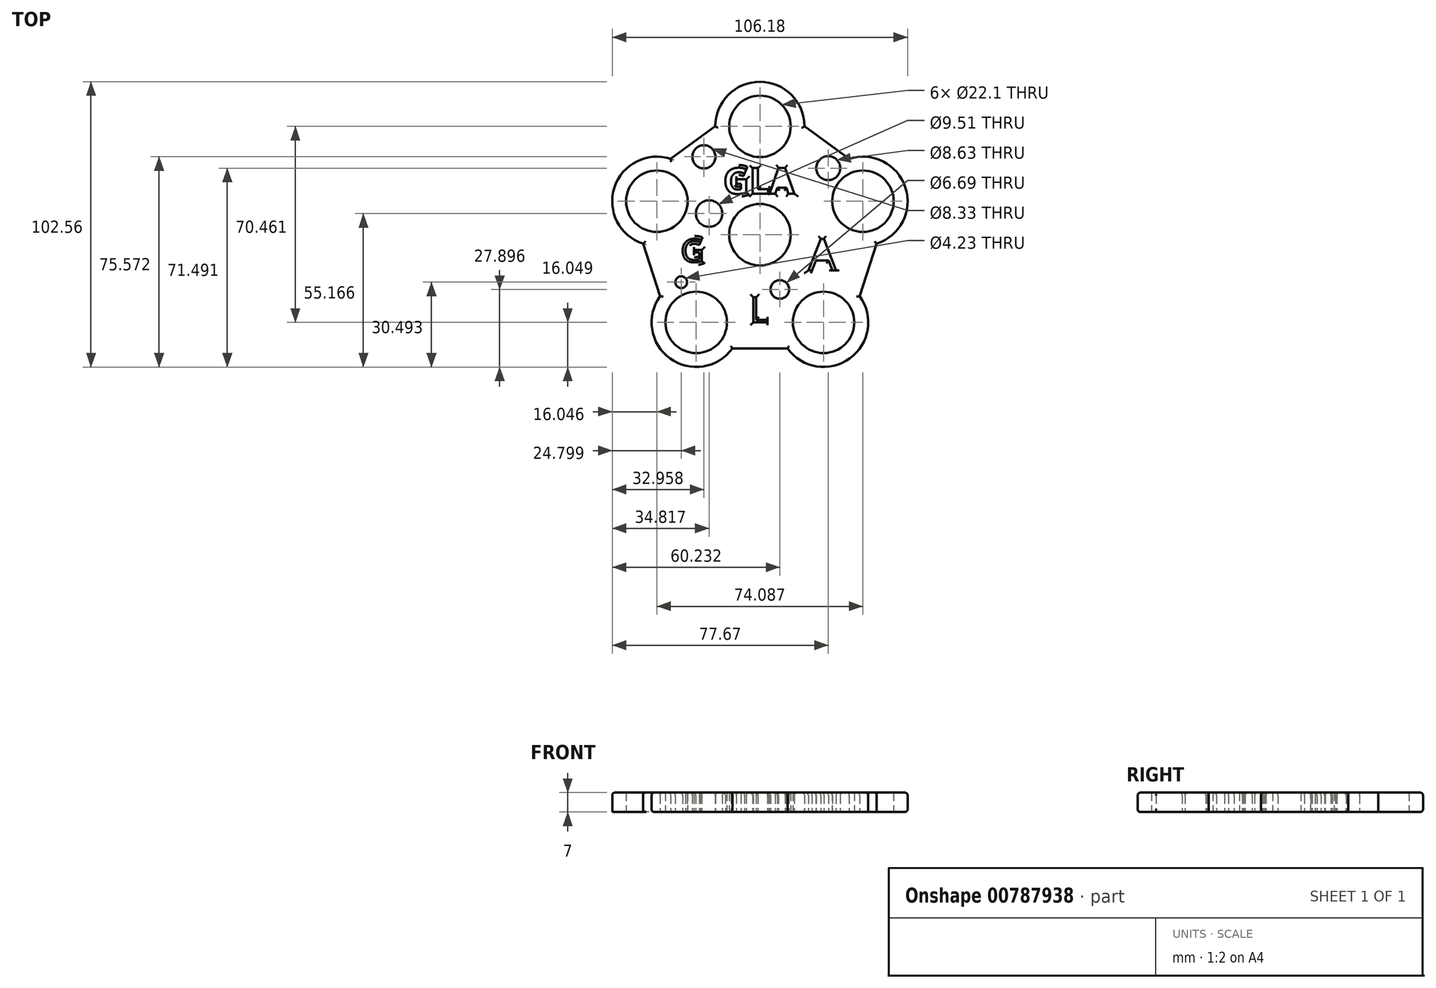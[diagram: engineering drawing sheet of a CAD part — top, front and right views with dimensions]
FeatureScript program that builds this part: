
annotation { "Feature Type Name" : "Feature", "Feature Type Description" : "" }
export const myFeature = defineFeature(function(context is Context, id is Id, definition is map)
    precondition{}
    {
        {
            var Q0;
            Q0=qCreatedBy(makeId("Top.planeOp"),FACE);
            var sketch = newSketch(context, id + "F0", { "sketchPlane" : qUnion([Q0])});
            skCircle(sketch, "E0", {"center": v(0, 0) * mm, "radius": 11.05 * mm});
            skCircle(sketch, "E1", {"center": v(0, 38.95) * mm, "radius": 11.05 * mm});
            skArc(sketch, "E2", {"start": v(16.05, 38.95) * mm, "mid": v(0, 55) * mm, "end": v(-16.05, 38.95) * mm});
            skCircle(sketch, "E3.1.0", {"center": v(-37.04, 12.04) * mm, "radius": 11.05 * mm});
            skArc(sketch, "E3.1.1", {"start": v(-32.08, 27.3) * mm, "mid": v(-52.3, 17) * mm, "end": v(-42, -3.23) * mm});
            skCircle(sketch, "E3.2.0", {"center": v(-22.9, -31.51) * mm, "radius": 11.05 * mm});
            skArc(sketch, "E3.2.1", {"start": v(-35.88, -22.08) * mm, "mid": v(-32.33, -44.5) * mm, "end": v(-9.9, -40.95) * mm});
            skCircle(sketch, "E3.3.0", {"center": v(22.9, -31.51) * mm, "radius": 11.05 * mm});
            skArc(sketch, "E3.3.1", {"start": v(9.9, -40.95) * mm, "mid": v(32.33, -44.5) * mm, "end": v(35.88, -22.08) * mm});
            skCircle(sketch, "E3.4.0", {"center": v(37.04, 12.04) * mm, "radius": 11.05 * mm});
            skArc(sketch, "E3.4.1", {"start": v(42, -3.23) * mm, "mid": v(52.3, 17) * mm, "end": v(32.08, 27.3) * mm});
            skLineSegment(sketch, "E4", {"start": v(-32.08, 27.3) * mm, "end": v(-32.08, 27.3) * mm});
            skLineSegment(sketch, "E5", {"start": v(-42, -3.23) * mm, "end": v(-35.88, -22.08) * mm, "construction": true});
            skLineSegment(sketch, "E6", {"start": v(-9.9, -40.95) * mm, "end": v(9.9, -40.95) * mm, "construction": true});
            skLineSegment(sketch, "E7", {"start": v(16.05, 38.95) * mm, "end": v(32.08, 27.3) * mm, "construction": true});
            skLineSegment(sketch, "E8", {"start": v(-16.05, 38.95) * mm, "end": v(-16.05, 38.95) * mm});
            skLineSegment(sketch, "E9", {"start": v(-32.08, 27.3) * mm, "end": v(-16.05, 38.95) * mm, "construction": true});
            skLineSegment(sketch, "E10", {"start": v(-32.08, 27.3) * mm, "end": v(-16.05, 38.95) * mm});
            skLineSegment(sketch, "E11", {"start": v(16.05, 38.95) * mm, "end": v(32.08, 27.3) * mm});
            skLineSegment(sketch, "E12", {"start": v(42, -3.23) * mm, "end": v(35.88, -22.08) * mm});
            skLineSegment(sketch, "E13", {"start": v(9.9, -40.95) * mm, "end": v(-9.9, -40.95) * mm});
            skLineSegment(sketch, "E14", {"start": v(-35.88, -22.08) * mm, "end": v(-42, -3.23) * mm});
            skText(sketch, "E15", { "text": "GLA", "fontName": "OpenSans-Bold.ttf"});
            skText(sketch, "E16", { "text": "G", "fontName": "OpenSans-Regular.ttf"});
            skText(sketch, "E17", { "text": "L", "fontName": "OpenSans-Regular.ttf"});
            skText(sketch, "E18", { "text": "A", "fontName": "OpenSans-Regular.ttf"});
            skCircle(sketch, "E19", {"center": v(-18.27, 7.6) * mm, "radius": 4.76 * mm});
            skCircle(sketch, "E20", {"center": v(24.58, 23.93) * mm, "radius": 4.31 * mm});
            skCircle(sketch, "E21", {"center": v(7.14, -19.66) * mm, "radius": 3.34 * mm});
            skCircle(sketch, "E22", {"center": v(-20.13, 28.01) * mm, "radius": 4.17 * mm});
            skCircle(sketch, "E23", {"center": v(-28.3, -17.07) * mm, "radius": 2.12 * mm});
            const initialGuessF0  = {"E15": [-0.01317, 0.01475, 1, 0, 0.00928], "E16": [-0.02848, -0.00983, 1, 0, 0.00835], "E17": [-0.00362, -0.03151, 1, 0, 0.0091], "E18": [0.01742, -0.01285, 1, 0, 0.01134]};
            skSetInitialGuess(sketch, initialGuessF0);
            skSolve(sketch);
        }
        {
            var Q0;
            Q0 = qSketchRegion(id + "F0", true);
            extrude(context, id + "F1", {"entities" : qUnion([Q0]), "depth" : 7 * mm, "offsetDistance" : 25 * mm});
        }
        {
            var Q0;
            Q0=makeQuery(id+"F1.opExtrude","CAP_EDGE",EDGE,{"disambiguationData":[OSD([sQuery(id+"F0.wireOp",EDGE,"E10")])],"isStart":false});
            var Q1;
            Q1=makeQuery(id+"F1.opExtrude","CAP_EDGE",EDGE,{"disambiguationData":[OSD([sQuery(id+"F0.wireOp",EDGE,"E3.1.1")])],"isStart":false});
            var Q2;
            Q2=makeQuery(id+"F1.opExtrude","CAP_EDGE",EDGE,{"disambiguationData":[OSD([sQuery(id+"F0.wireOp",EDGE,"E14")])],"isStart":false});
            var Q3;
            Q3=makeQuery(id+"F1.opExtrude","CAP_EDGE",EDGE,{"disambiguationData":[OSD([sQuery(id+"F0.wireOp",EDGE,"E3.2.1")])],"isStart":false});
            var Q4;
            Q4=makeQuery(id+"F1.opExtrude","CAP_EDGE",EDGE,{"disambiguationData":[OSD([sQuery(id+"F0.wireOp",EDGE,"E13")])],"isStart":false});
            var Q5;
            Q5=makeQuery(id+"F1.opExtrude","CAP_EDGE",EDGE,{"disambiguationData":[OSD([sQuery(id+"F0.wireOp",EDGE,"E3.3.1")])],"isStart":false});
            var Q6;
            Q6=makeQuery(id+"F1.opExtrude","CAP_EDGE",EDGE,{"disambiguationData":[OSD([sQuery(id+"F0.wireOp",EDGE,"E12")])],"isStart":false});
            var Q7;
            Q7=makeQuery(id+"F1.opExtrude","CAP_EDGE",EDGE,{"disambiguationData":[OSD([sQuery(id+"F0.wireOp",EDGE,"E3.4.1")])],"isStart":false});
            var Q8;
            Q8=makeQuery(id+"F1.opExtrude","CAP_EDGE",EDGE,{"disambiguationData":[OSD([sQuery(id+"F0.wireOp",EDGE,"E11")])],"isStart":false});
            var Q9;
            Q9=makeQuery(id+"F1.opExtrude","CAP_EDGE",EDGE,{"disambiguationData":[OSD([sQuery(id+"F0.wireOp",EDGE,"E2")])],"isStart":false});
            var Q10;
            Q10=makeQuery(id+"F1.opExtrude","CAP_EDGE",EDGE,{"disambiguationData":[OSD([sQuery(id+"F0.wireOp",EDGE,"E10")])],"isStart":true});
            var Q11;
            Q11=makeQuery(id+"F1.opExtrude","CAP_EDGE",EDGE,{"disambiguationData":[OSD([sQuery(id+"F0.wireOp",EDGE,"E2")])],"isStart":true});
            var Q12;
            Q12=makeQuery(id+"F1.opExtrude","CAP_EDGE",EDGE,{"disambiguationData":[OSD([sQuery(id+"F0.wireOp",EDGE,"E11")])],"isStart":true});
            var Q13;
            Q13=makeQuery(id+"F1.opExtrude","CAP_EDGE",EDGE,{"disambiguationData":[OSD([sQuery(id+"F0.wireOp",EDGE,"E3.4.1")])],"isStart":true});
            var Q14;
            Q14=makeQuery(id+"F1.opExtrude","CAP_EDGE",EDGE,{"disambiguationData":[OSD([sQuery(id+"F0.wireOp",EDGE,"E12")])],"isStart":true});
            var Q15;
            Q15=makeQuery(id+"F1.opExtrude","CAP_EDGE",EDGE,{"disambiguationData":[OSD([sQuery(id+"F0.wireOp",EDGE,"E3.3.1")])],"isStart":true});
            var Q16;
            Q16=makeQuery(id+"F1.opExtrude","CAP_EDGE",EDGE,{"disambiguationData":[OSD([sQuery(id+"F0.wireOp",EDGE,"E13")])],"isStart":true});
            var Q17;
            Q17=makeQuery(id+"F1.opExtrude","CAP_EDGE",EDGE,{"disambiguationData":[OSD([sQuery(id+"F0.wireOp",EDGE,"E3.2.1")])],"isStart":true});
            var Q18;
            Q18=makeQuery(id+"F1.opExtrude","CAP_EDGE",EDGE,{"disambiguationData":[OSD([sQuery(id+"F0.wireOp",EDGE,"E14")])],"isStart":true});
            var Q19;
            Q19=makeQuery(id+"F1.opExtrude","CAP_EDGE",EDGE,{"disambiguationData":[OSD([sQuery(id+"F0.wireOp",EDGE,"E23")])],"isStart":false});
            var Q20;
            Q20=makeQuery(id+"F1.opExtrude","CAP_EDGE",EDGE,{"disambiguationData":[OSD([sQuery(id+"F0.wireOp",EDGE,"E21")])],"isStart":false});
            var Q21;
            Q21=makeQuery(id+"F1.opExtrude","CAP_EDGE",EDGE,{"disambiguationData":[OSD([sQuery(id+"F0.wireOp",EDGE,"E20")])],"isStart":false});
            var Q22;
            Q22=makeQuery(id+"F1.opExtrude","CAP_EDGE",EDGE,{"disambiguationData":[OSD([sQuery(id+"F0.wireOp",EDGE,"E15.sketch_text.stroke-19")])],"isStart":false});
            var Q23;
            Q23=makeQuery(id+"F1.opExtrude","CAP_EDGE",EDGE,{"disambiguationData":[OSD([sQuery(id+"F0.wireOp",EDGE,"E15.sketch_text.stroke-21")])],"isStart":false});
            var Q24;
            Q24=makeQuery(id+"F1.opExtrude","CAP_EDGE",EDGE,{"disambiguationData":[OSD([sQuery(id+"F0.wireOp",EDGE,"E15.sketch_text.stroke-20")])],"isStart":false});
            var Q25;
            Q25=makeQuery(id+"F1.opExtrude","CAP_EDGE",EDGE,{"disambiguationData":[OSD([sQuery(id+"F0.wireOp",EDGE,"E15.sketch_text.stroke-22")])],"isStart":false});
            var Q26;
            Q26=makeQuery(id+"F1.opExtrude","CAP_EDGE",EDGE,{"disambiguationData":[OSD([sQuery(id+"F0.wireOp",EDGE,"E15.sketch_text.stroke-24")])],"isStart":false});
            var Q27;
            Q27=makeQuery(id+"F1.opExtrude","CAP_EDGE",EDGE,{"disambiguationData":[OSD([sQuery(id+"F0.wireOp",EDGE,"E15.sketch_text.stroke-23")])],"isStart":false});
            var Q28;
            Q28=makeQuery(id+"F1.opExtrude","CAP_EDGE",EDGE,{"disambiguationData":[OSD([sQuery(id+"F0.wireOp",EDGE,"E15.sketch_text.stroke-29")])],"isStart":false});
            var Q29;
            Q29=makeQuery(id+"F1.opExtrude","CAP_EDGE",EDGE,{"disambiguationData":[OSD([sQuery(id+"F0.wireOp",EDGE,"E15.sketch_text.stroke-30")])],"isStart":false});
            var Q30;
            Q30=makeQuery(id+"F1.opExtrude","CAP_EDGE",EDGE,{"disambiguationData":[OSD([sQuery(id+"F0.wireOp",EDGE,"E15.sketch_text.stroke-31")])],"isStart":false});
            var Q31;
            Q31=makeQuery(id+"F1.opExtrude","CAP_EDGE",EDGE,{"disambiguationData":[OSD([sQuery(id+"F0.wireOp",EDGE,"E15.sketch_text.stroke-26")])],"isStart":false});
            var Q32;
            Q32=makeQuery(id+"F1.opExtrude","CAP_EDGE",EDGE,{"disambiguationData":[OSD([sQuery(id+"F0.wireOp",EDGE,"E15.sketch_text.stroke-28")])],"isStart":false});
            var Q33;
            Q33=makeQuery(id+"F1.opExtrude","CAP_EDGE",EDGE,{"disambiguationData":[OSD([sQuery(id+"F0.wireOp",EDGE,"E15.sketch_text.stroke-27")])],"isStart":false});
            var Q34;
            Q34=makeQuery(id+"F1.opExtrude","CAP_EDGE",EDGE,{"disambiguationData":[OSD([sQuery(id+"F0.wireOp",EDGE,"E19")])],"isStart":false});
            var Q35;
            Q35=makeQuery(id+"F1.opExtrude","CAP_EDGE",EDGE,{"disambiguationData":[OSD([sQuery(id+"F0.wireOp",EDGE,"E22")])],"isStart":false});
            var Q36;
            Q36=makeQuery(id+"F1.opExtrude","CAP_EDGE",EDGE,{"disambiguationData":[OSD([sQuery(id+"F0.wireOp",EDGE,"E15.sketch_text.stroke-25")])],"isStart":false});
            var Q37;
            Q37=makeQuery(id+"F1.opExtrude","CAP_EDGE",EDGE,{"disambiguationData":[OSD([sQuery(id+"F0.wireOp",EDGE,"E15.sketch_text.stroke-32")])],"isStart":false});
            var Q38;
            Q38=makeQuery(id+"F1.opExtrude","CAP_EDGE",EDGE,{"disambiguationData":[OSD([sQuery(id+"F0.wireOp",EDGE,"E17.sketch_text.stroke-0")])],"isStart":false});
            var Q39;
            Q39=makeQuery(id+"F1.opExtrude","CAP_EDGE",EDGE,{"disambiguationData":[OSD([sQuery(id+"F0.wireOp",EDGE,"E17.sketch_text.stroke-1")])],"isStart":false});
            var Q40;
            Q40=makeQuery(id+"F1.opExtrude","CAP_EDGE",EDGE,{"disambiguationData":[OSD([sQuery(id+"F0.wireOp",EDGE,"E17.sketch_text.stroke-2")])],"isStart":false});
            var Q41;
            Q41=makeQuery(id+"F1.opExtrude","CAP_EDGE",EDGE,{"disambiguationData":[OSD([sQuery(id+"F0.wireOp",EDGE,"E17.sketch_text.stroke-3")])],"isStart":false});
            var Q42;
            Q42=makeQuery(id+"F1.opExtrude","CAP_EDGE",EDGE,{"disambiguationData":[OSD([sQuery(id+"F0.wireOp",EDGE,"E17.sketch_text.stroke-5")])],"isStart":false});
            var Q43;
            Q43=makeQuery(id+"F1.opExtrude","CAP_EDGE",EDGE,{"disambiguationData":[OSD([sQuery(id+"F0.wireOp",EDGE,"E18.sketch_text.stroke-1")])],"isStart":false});
            var Q44;
            Q44=makeQuery(id+"F1.opExtrude","CAP_EDGE",EDGE,{"disambiguationData":[OSD([sQuery(id+"F0.wireOp",EDGE,"E18.sketch_text.stroke-0")])],"isStart":false});
            var Q45;
            Q45=makeQuery(id+"F1.opExtrude","CAP_EDGE",EDGE,{"disambiguationData":[OSD([sQuery(id+"F0.wireOp",EDGE,"E18.sketch_text.stroke-4")])],"isStart":false});
            var Q46;
            Q46=makeQuery(id+"F1.opExtrude","CAP_EDGE",EDGE,{"disambiguationData":[OSD([sQuery(id+"F0.wireOp",EDGE,"E18.sketch_text.stroke-5")])],"isStart":false});
            var Q47;
            Q47=makeQuery(id+"F1.opExtrude","CAP_EDGE",EDGE,{"disambiguationData":[OSD([sQuery(id+"F0.wireOp",EDGE,"E18.sketch_text.stroke-6")])],"isStart":false});
            var Q48;
            Q48=makeQuery(id+"F1.opExtrude","CAP_EDGE",EDGE,{"disambiguationData":[OSD([sQuery(id+"F0.wireOp",EDGE,"E18.sketch_text.stroke-3")])],"isStart":false});
            var Q49;
            Q49=makeQuery(id+"F1.opExtrude","CAP_EDGE",EDGE,{"disambiguationData":[OSD([sQuery(id+"F0.wireOp",EDGE,"E16.sketch_text.stroke-8")])],"isStart":false});
            var Q50;
            Q50=makeQuery(id+"F1.opExtrude","CAP_EDGE",EDGE,{"disambiguationData":[OSD([sQuery(id+"F0.wireOp",EDGE,"E16.sketch_text.stroke-11")])],"isStart":false});
            var Q51;
            Q51=makeQuery(id+"F1.opExtrude","CAP_EDGE",EDGE,{"disambiguationData":[OSD([sQuery(id+"F0.wireOp",EDGE,"E16.sketch_text.stroke-1")])],"isStart":false});
            var Q52;
            Q52=makeQuery(id+"F1.opExtrude","CAP_EDGE",EDGE,{"disambiguationData":[OSD([sQuery(id+"F0.wireOp",EDGE,"E16.sketch_text.stroke-0")])],"isStart":false});
            var Q53;
            Q53=makeQuery(id+"F1.opExtrude","CAP_EDGE",EDGE,{"disambiguationData":[OSD([sQuery(id+"F0.wireOp",EDGE,"E16.sketch_text.stroke-18")])],"isStart":false});
            var Q54;
            Q54=makeQuery(id+"F1.opExtrude","CAP_EDGE",EDGE,{"disambiguationData":[OSD([sQuery(id+"F0.wireOp",EDGE,"E15.sketch_text.stroke-6")])],"isStart":false});
            var Q55;
            Q55=makeQuery(id+"F1.opExtrude","CAP_EDGE",EDGE,{"disambiguationData":[OSD([sQuery(id+"F0.wireOp",EDGE,"E15.sketch_text.stroke-12")])],"isStart":false});
            var Q56;
            Q56=makeQuery(id+"F1.opExtrude","CAP_EDGE",EDGE,{"disambiguationData":[OSD([sQuery(id+"F0.wireOp",EDGE,"E15.sketch_text.stroke-15")])],"isStart":false});
            var Q57;
            Q57=makeQuery(id+"F1.opExtrude","CAP_EDGE",EDGE,{"disambiguationData":[OSD([sQuery(id+"F0.wireOp",EDGE,"E15.sketch_text.stroke-1")])],"isStart":false});
            var Q58;
            Q58=makeQuery(id+"F1.opExtrude","CAP_EDGE",EDGE,{"disambiguationData":[OSD([sQuery(id+"F0.wireOp",EDGE,"E15.sketch_text.stroke-0")])],"isStart":false});
            var Q59;
            Q59=makeQuery(id+"F1.opExtrude","CAP_EDGE",EDGE,{"disambiguationData":[OSD([sQuery(id+"F0.wireOp",EDGE,"E15.sketch_text.stroke-17")])],"isStart":false});
            fillet(context, id + "F2", {"entities" : qUnion([Q0, Q1, Q2, Q3, Q4, Q5, Q6, Q7, Q8, Q9, Q10, Q11, Q12, Q13, Q14, Q15, Q16, Q17, Q18, Q19, Q20, Q21, Q22, Q23, Q24, Q25, Q26, Q27, Q28, Q29, Q30, Q31, Q32, Q33, Q34, Q35, Q36, Q37, Q38, Q39, Q40, Q41, Q42, Q43, Q44, Q45, Q46, Q47, Q48, Q49, Q50, Q51, Q52, Q53, Q54, Q55, Q56, Q57, Q58, Q59]), "radius" : 1 * mm, "tangentPropagation" : true, "allowEdgeOverflow" : false});
        }
    });
